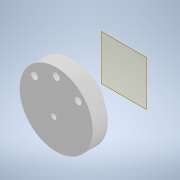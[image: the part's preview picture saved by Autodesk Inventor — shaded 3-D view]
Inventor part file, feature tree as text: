
AUTODESK INVENTOR PART (.ipt)
format: ipt  version: 2022 (Build 260153000, 153)  size: 181,248 bytes
history: native  units: mm
features: extrude x8, sketch x8, other x5, reference x4, chamfer x1, mirror x1, projected_geometry x1
ambient origin geometry x8: Origin, YZ Plane, XZ Plane, XY Plane, X Axis, Y Axis, Z Axis, Center Point
bodies: Body1 (feature_tree)
feature tree (28):
  other  "Твердое тело1"
  extrude  "Выдавливание1"  Depth=45.0mm
  extrude  "Выдавливание2"  Depth=9.295mm TaperAngle=0.0deg
  extrude  "Выдавливание3"  Depth=25.2mm
  chamfer  "Фаска1"  Distance=7.8mm
  extrude  "Выдавливание4"  Depth=2.0mm
  extrude  "Выдавливание5"  Depth=1.0mm TaperAngle=0.0deg
  extrude  "Выдавливание6"  Depth=0.5mm TaperAngle=45.0deg
  extrude  "Выдавливание7"  Depth=4.0mm
  other  "РабПлоскость1"
  mirror  "Зеркальное отражение1"
  extrude  "Выдавливание8"  Depth=0.5mm
  sketch  "Эскиз1"
  sketch  "Эскиз2"
  sketch  "Эскиз3"
  projected_geometry  "Спроецированная петля1"
  sketch  "Эскиз4"
  sketch  "Эскиз5"
  reference  "Ссылка1"
  reference  "Ссылка2"
  reference  "Ссылка3"
  sketch  "Эскиз6"
  reference  "Ссылка4"
  sketch  "Эскиз7"
  sketch  "Эскиз8"
  other  "<userpath>\Documents\Git\MZCAT_2024\MZCAT.iam"
  other  "MZCAT.iam"
  other  "base plate:2"
